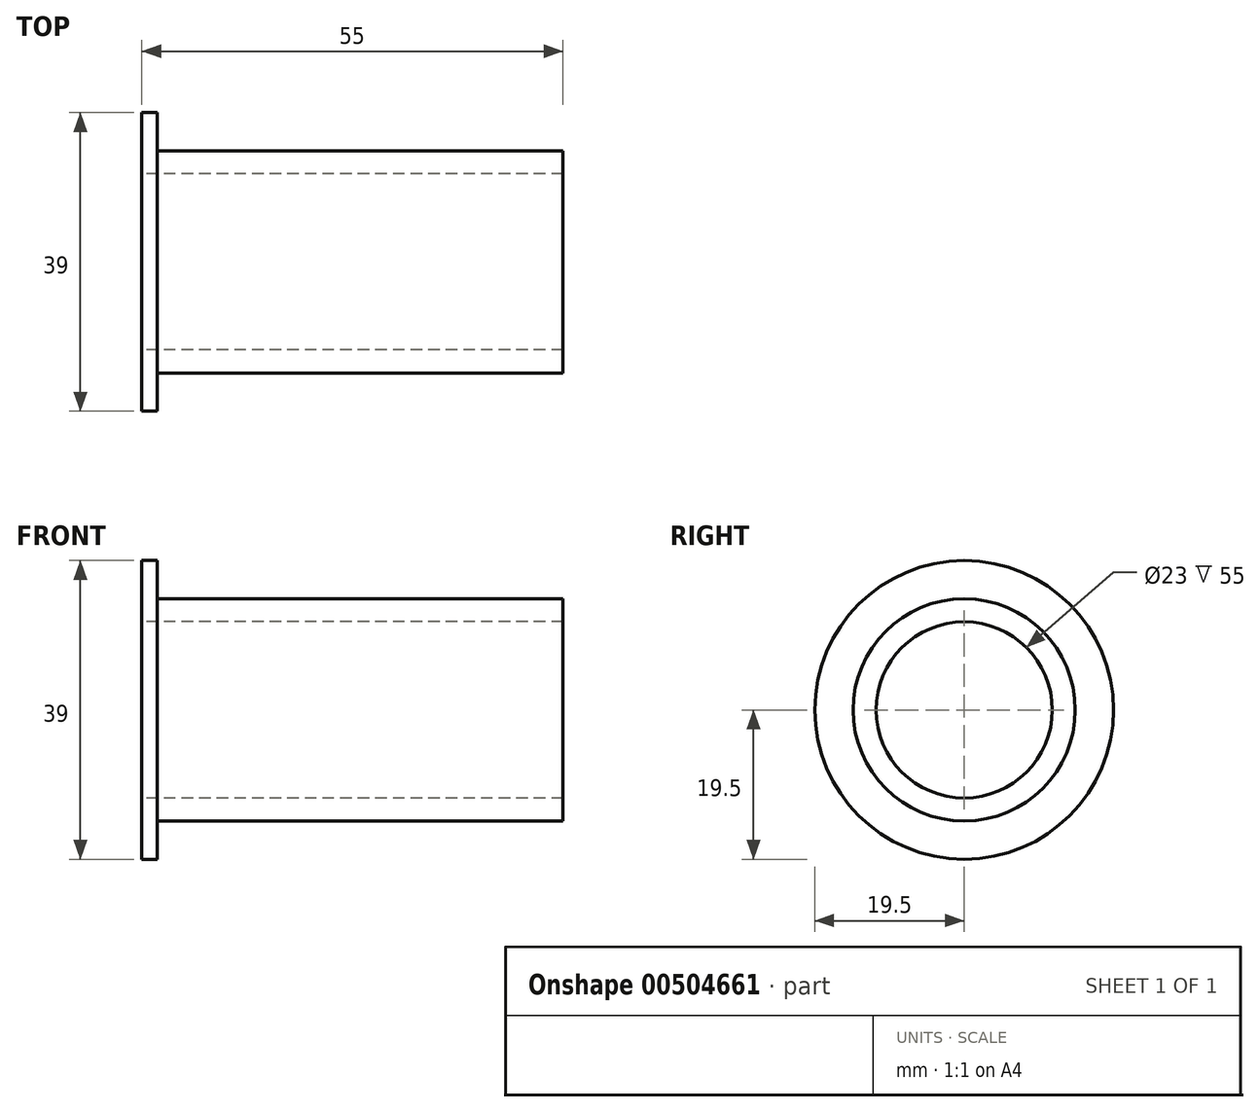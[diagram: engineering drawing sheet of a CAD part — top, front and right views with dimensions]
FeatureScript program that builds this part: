
annotation { "Feature Type Name" : "Feature", "Feature Type Description" : "" }
export const myFeature = defineFeature(function(context is Context, id is Id, definition is map)
    precondition{}
    {
        {
            var Q0;
            Q0=qCreatedBy(makeId("Front.planeOp"),FACE);
            var sketch = newSketch(context, id + "F0", { "sketchPlane" : qUnion([Q0])});
            skLineSegment(sketch, "E0.bottom", {"start": v(0, 19.5) * mm, "end": v(2, 19.5) * mm});
            skLineSegment(sketch, "E0.top", {"start": v(0, 11.5) * mm, "end": v(2, 11.5) * mm});
            skLineSegment(sketch, "E0.left", {"start": v(0, 19.5) * mm, "end": v(0, 11.5) * mm});
            skLineSegment(sketch, "E0.right", {"start": v(2, 19.5) * mm, "end": v(2, 14.5) * mm});
            skLineSegment(sketch, "E1.bottom", {"start": v(2, 11.5) * mm, "end": v(55, 11.5) * mm});
            skLineSegment(sketch, "E1.top", {"start": v(2, 14.5) * mm, "end": v(55, 14.5) * mm});
            skLineSegment(sketch, "E1.right", {"start": v(55, 11.5) * mm, "end": v(55, 14.5) * mm});
            skLineSegment(sketch, "E2", {"start": v(0, 0) * mm, "end": v(76.39, 0) * mm, "construction": true});
            skSolve(sketch);
        }
        {
            var Q0;
            Q0 = qSketchRegion(id + "F0", true);
            var Q1;
            Q1=sQuery(id+"F0.wireOp",EDGE,"E2");
            revolve(context, id + "F1", {"entities" : qUnion([Q0]), "axis" : qUnion([Q1]), "revolveType" : RevolveType.FULL});
        }
    });
